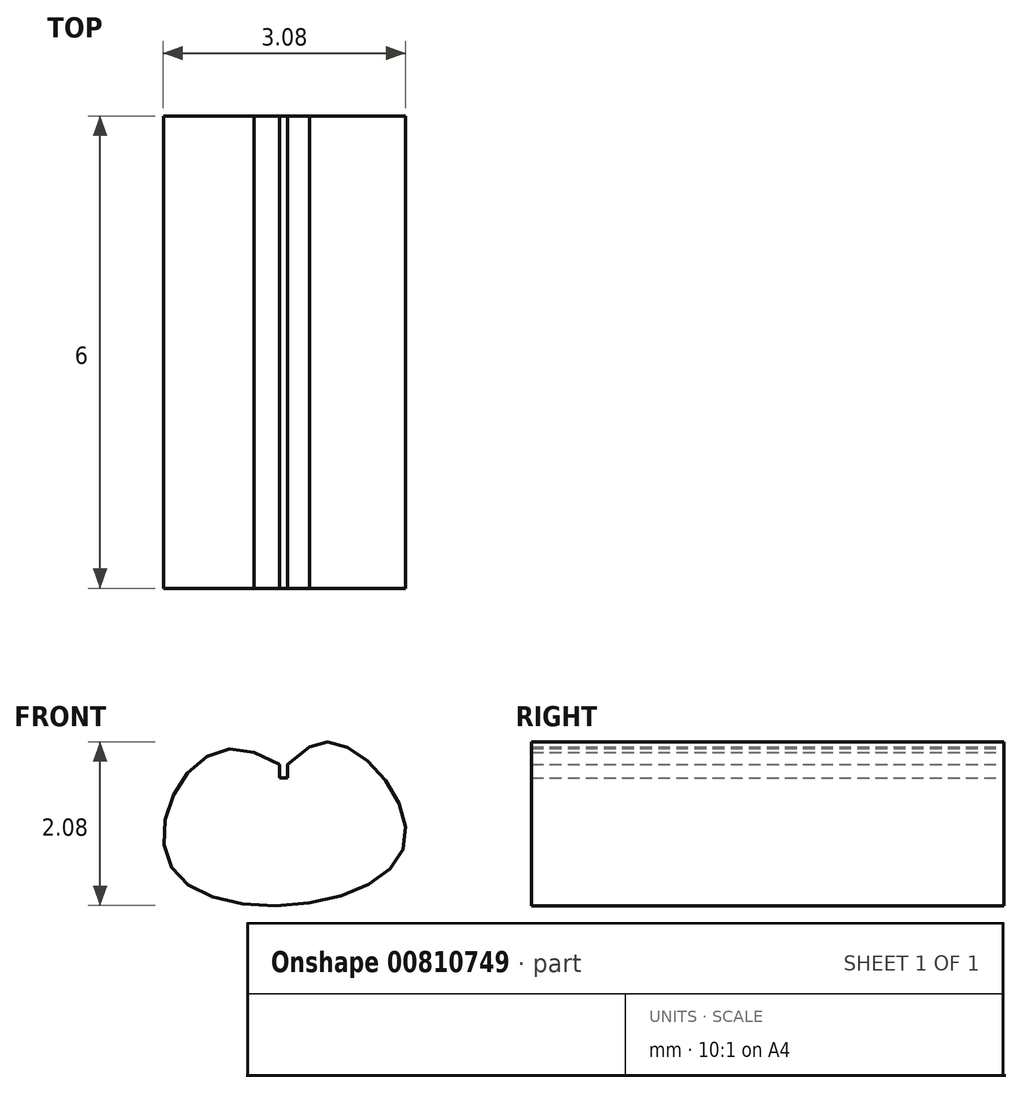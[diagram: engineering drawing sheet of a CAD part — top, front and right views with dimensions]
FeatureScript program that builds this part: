
annotation { "Feature Type Name" : "Feature", "Feature Type Description" : "" }
export const myFeature = defineFeature(function(context is Context, id is Id, definition is map)
    precondition{}
    {
        {
            var Q0;
            Q0=qCreatedBy(makeId("Front.planeOp"),FACE);
            var sketch = newSketch(context, id + "F0", { "sketchPlane" : qUnion([Q0])});
            skLineSegment(sketch, "E0", {"start": v(0, 0) * mm, "end": v(-0.32, 0.16) * mm});
            skLineSegment(sketch, "E1", {"start": v(0, 0) * mm, "end": v(0, -0.17) * mm});
            skLineSegment(sketch, "E2", {"start": v(0.1, -0.17) * mm, "end": v(0.1, 0) * mm});
            skLineSegment(sketch, "E3", {"start": v(0.1, 0) * mm, "end": v(0.38, 0.22) * mm});
            skLineSegment(sketch, "E4", {"start": v(0, -0.17) * mm, "end": v(0.1, -0.17) * mm});
            skFitSpline(sketch, "E5", {"points": [v(-0.32, 0.16) * mm, v(-1.37, -1.32) * mm, v(1.57, -1.07) * mm, v(0.38, 0.22) * mm], "startDerivative": vector(-7.39, 2.97) * mm, "endDerivative": vector(-4.65, -3.21) * mm});
            skLineSegment(sketch, "E6.0", {"start": v(-0.2, -0.13) * mm, "end": v(-0.4, -0.03) * mm});
            skLineSegment(sketch, "E6.1", {"start": v(0.3, -0.1) * mm, "end": v(0.5, 0.06) * mm});
            skLineSegment(sketch, "E6.2", {"start": v(0.3, -0.37) * mm, "end": v(0.3, -0.1) * mm});
            skFitSpline(sketch, "E6.3", {"points": [v(-0.4, -0.03) * mm, v(-0.46, 0) * mm, v(-0.56, 0.01) * mm, v(-0.7, 0) * mm, v(-0.85, -0.08) * mm, v(-1.04, -0.24) * mm, v(-1.2, -0.49) * mm, v(-1.27, -0.75) * mm, v(-1.28, -0.94) * mm, v(-1.25, -1.1) * mm, v(-1.19, -1.24) * mm, v(-1.07, -1.35) * mm, v(-0.9, -1.45) * mm, v(-0.68, -1.53) * mm, v(-0.34, -1.6) * mm, v(0.15, -1.6) * mm, v(0.62, -1.52) * mm, v(0.94, -1.4) * mm, v(1.14, -1.29) * mm, v(1.3, -1.17) * mm, v(1.37, -1.04) * mm, v(1.4, -0.92) * mm, v(1.4, -0.76) * mm, v(1.34, -0.58) * mm, v(1.2, -0.33) * mm, v(1.01, -0.11) * mm, v(0.8, 0.03) * mm, v(0.66, 0.09) * mm, v(0.56, 0.1) * mm, v(0.52, 0.08) * mm, v(0.5, 0.06) * mm]});
            skLineSegment(sketch, "E6.4", {"start": v(-0.2, -0.37) * mm, "end": v(0.3, -0.37) * mm});
            skLineSegment(sketch, "E6.5", {"start": v(-0.2, -0.13) * mm, "end": v(-0.2, -0.37) * mm});
            skSolve(sketch);
        }
        {
            var Q0;
            Q0=makeQuery(id+"F0.imprint","IMPRINT",FACE,{"disambiguationData":[TD([[makeQuery(id+"F0.imprint","IMPRINT",EDGE,{"derivedFrom":sQuery(id+"F0.wireOp",EDGE,"E0")}),1.0]])]});
            extrude(context, id + "F1", {"entities" : qUnion([Q0]), "depth" : 6 * mm, "offsetDistance" : 25 * mm});
        }
    });
